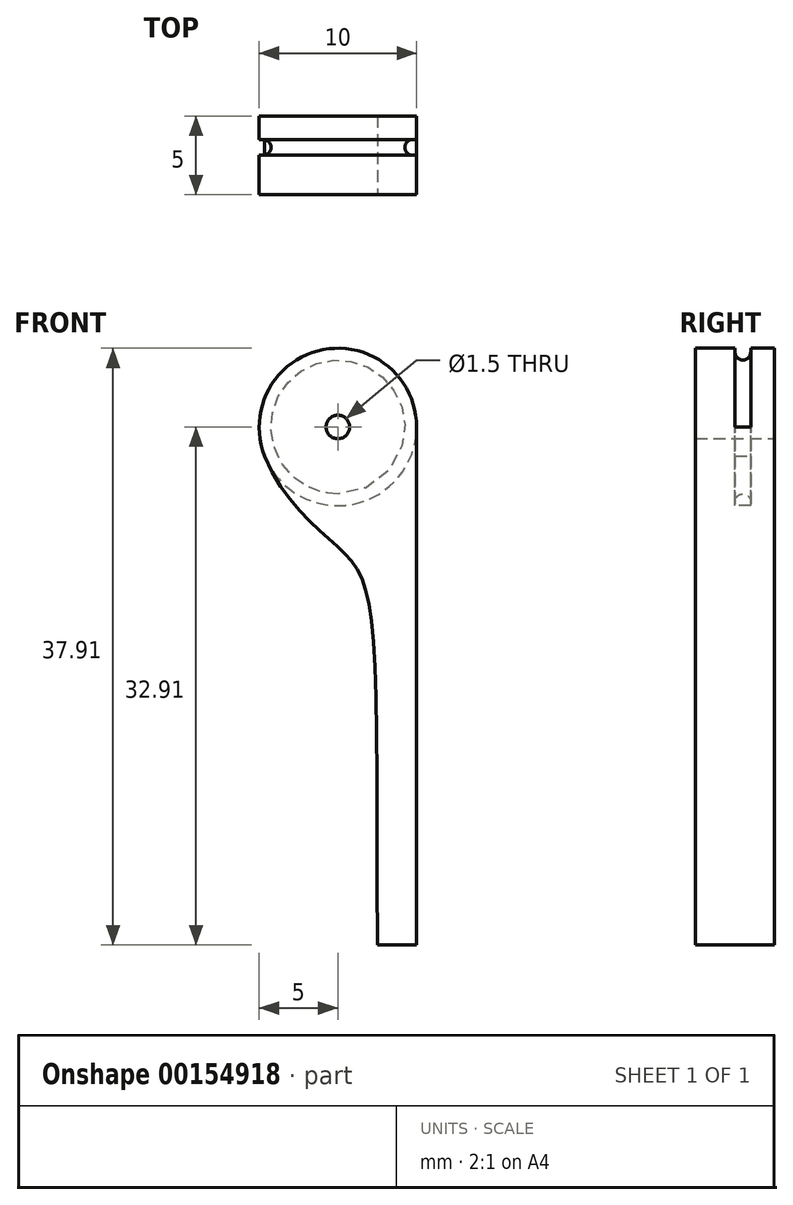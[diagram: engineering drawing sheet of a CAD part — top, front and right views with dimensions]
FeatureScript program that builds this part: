
annotation { "Feature Type Name" : "Feature", "Feature Type Description" : "" }
export const myFeature = defineFeature(function(context is Context, id is Id, definition is map)
    precondition{}
    {
        {
            var Q0;
            Q0=qCreatedBy(makeId("Front.planeOp"),FACE);
            var sketch = newSketch(context, id + "F0", { "sketchPlane" : qUnion([Q0])});
            skCircle(sketch, "E0", {"center": v(0, 0) * mm, "radius": 5 * mm});
            skLineSegment(sketch, "E1", {"start": v(5, 0) * mm, "end": v(5, -32.9) * mm});
            skLineSegment(sketch, "E2", {"start": v(5, -32.9) * mm, "end": v(2.5, -32.9) * mm});
            skFitSpline(sketch, "E3", {"points": [v(2.5, -32.9) * mm, v(0, -7.62) * mm, v(-4.65, -1.84) * mm], "startDerivative": vector(0, 100.43) * mm, "endDerivative": vector(-9.83, 24.9) * mm});
            skCircle(sketch, "E4", {"center": v(0, 0) * mm, "radius": 0.75 * mm});
            skSolve(sketch);
        }
        {
            var Q0;
            {var subQ0=sQuery(id+"F0.wireOp",EDGE,"E1");Q0=makeQuery(id+"F0.imprint","IMPRINT",FACE,{"disambiguationData":[TD([[makeQuery(id+"F0.imprint","IMPRINT",EDGE,{"derivedFrom":subQ0}),-1.0]])]});}
            var Q1;
            {var subQ0=sQuery(id+"F0.wireOp",EDGE,"E0");var subQ1=makeQuery(id+"F0.imprint","INTERSECT",VERTEX,{"derivedFrom":[subQ0,sQuery(id+"F0.wireOp",EDGE,"E1")]});Q1=makeQuery(id+"F0.imprint","IMPRINT",FACE,{"disambiguationData":[TD([[makeQuery(id+"F0.imprint","IMPRINT",EDGE,{"disambiguationData":[TD([[subQ1,-1.0]])],"derivedFrom":subQ0}),1.0]])]});}
            extrude(context, id + "F1", {"entities" : qUnion([Q0, Q1]), "depth" : 5 * mm});
        }
        {
            var Q0;
            Q0=qCreatedBy(makeId("Top.planeOp"),FACE);
            var sketch = newSketch(context, id + "F2", { "sketchPlane" : qUnion([Q0])});
            skLineSegment(sketch, "E5", {"start": v(0, 0) * mm, "end": v(0, -3.98) * mm, "construction": true});
            skLineSegment(sketch, "E6", {"start": v(0, -2) * mm, "end": v(5, -2) * mm, "construction": true});
            skLineSegment(sketch, "E7.bottom", {"start": v(5, -2.5) * mm, "end": v(4.75, -2.5) * mm});
            skLineSegment(sketch, "E7.top", {"start": v(5, -1.5) * mm, "end": v(4.75, -1.5) * mm});
            skLineSegment(sketch, "E7.left", {"start": v(5, -2.5) * mm, "end": v(5, -1.5) * mm});
            skLineSegment(sketch, "E7.right", {"start": v(4.75, -2.5) * mm, "end": v(4.75, -1.5) * mm});
            skArc(sketch, "E8", {"start": v(4.75, -1.5) * mm, "mid": v(4.25, -2) * mm, "end": v(4.75, -2.5) * mm});
            skSolve(sketch);
        }
        {
            var Q0;
            Q0 = qSketchRegion(id + "F2", true);
            var Q1;
            Q1=sQuery(id+"F2.wireOp",EDGE,"E5");
            revolve(context, id + "F3", {"operationType" : NewBodyOperationType.REMOVE, "entities" : qUnion([Q0]), "axis" : qUnion([Q1]), "revolveType" : RevolveType.FULL, "oppositeDirection" : true});
        }
    });
